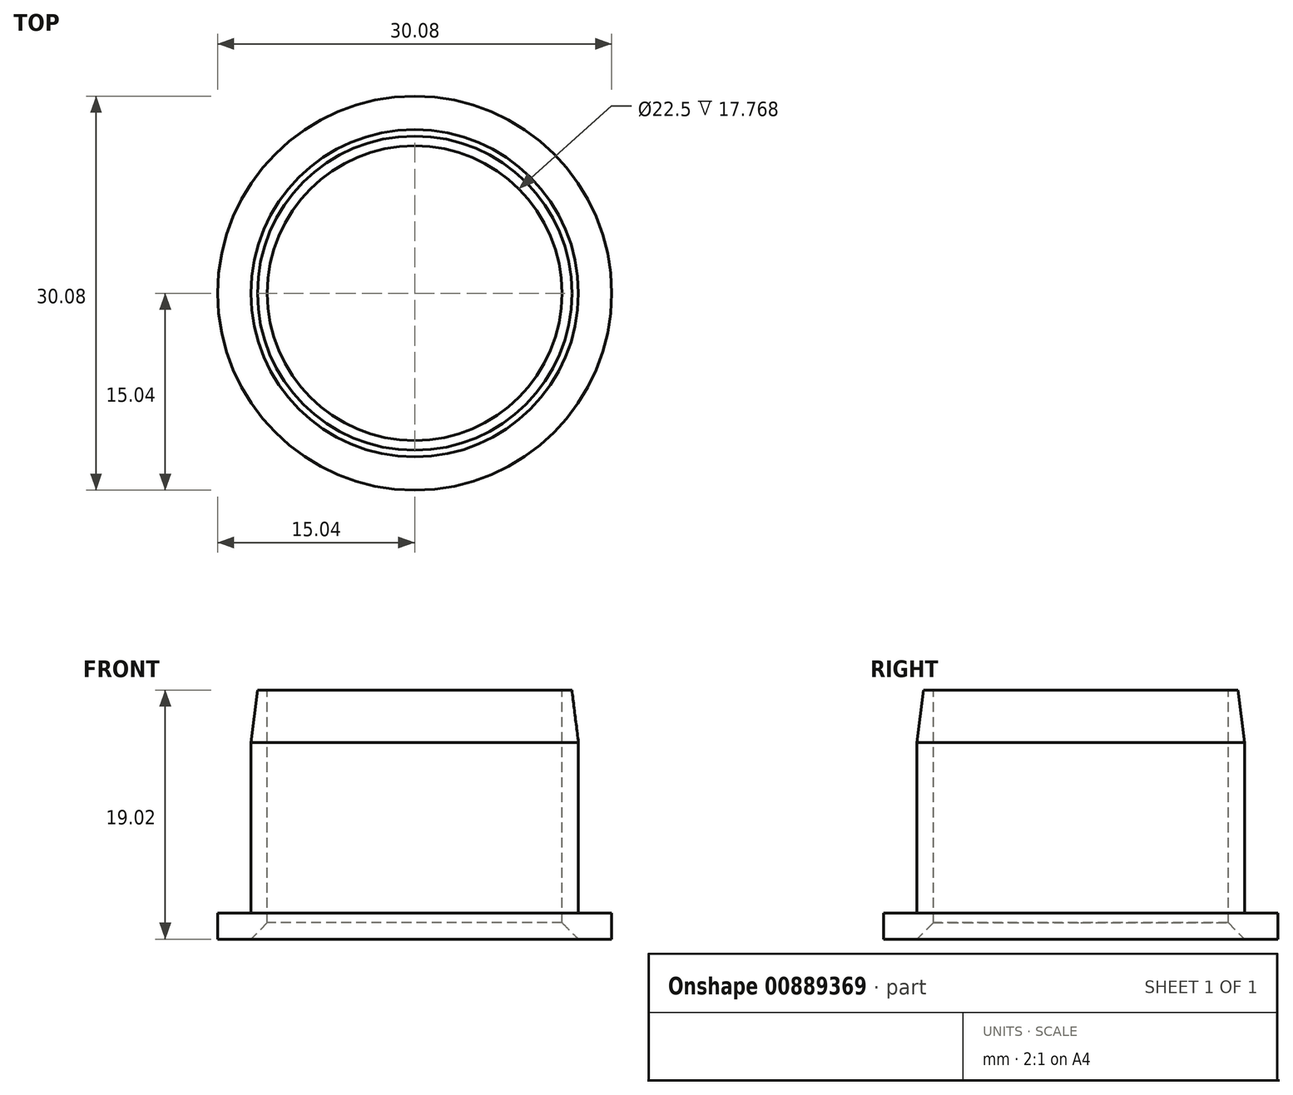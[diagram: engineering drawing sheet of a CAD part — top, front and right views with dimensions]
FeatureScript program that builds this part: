
annotation { "Feature Type Name" : "Feature", "Feature Type Description" : "" }
export const myFeature = defineFeature(function(context is Context, id is Id, definition is map)
    precondition{}
    {
        {
            assignVariable(context, id + "F0", {"name" : "H", "anyValue" : 17.02 * mm});
        }
        {
            var Q0;
            Q0=qCreatedBy(makeId("Top.planeOp"),FACE);
            var sketch = newSketch(context, id + "F1", { "sketchPlane" : qUnion([Q0])});
            skCircle(sketch, "E0", {"center": v(0, 0) * mm, "radius": 12.5 * mm});
            skCircle(sketch, "E1", {"center": v(0, 0) * mm, "radius": 11.25 * mm});
            skCircle(sketch, "E2", {"center": v(0, 0) * mm, "radius": 15.04 * mm});
            skSolve(sketch);
        }
        {
            var Q0;
            Q0=makeQuery(id+"F1.imprint","IMPRINT",FACE,{"disambiguationData":[TD([[makeQuery(id+"F1.imprint","IMPRINT",EDGE,{"derivedFrom":sQuery(id+"F1.wireOp",EDGE,"E0")}),-1.0]])]});
            var Q1;
            Q1=makeQuery(id+"F1.imprint","IMPRINT",FACE,{"disambiguationData":[TD([[makeQuery(id+"F1.imprint","IMPRINT",EDGE,{"derivedFrom":sQuery(id+"F1.wireOp",EDGE,"E0")}),1.0]])]});
            extrude(context, id + "F2", {"entities" : qUnion([Q0, Q1]), "oppositeDirection" : true, "depth" : 2 * mm, "offsetDistance" : 25.4 * mm});
        }
        {
            var Q0;
            Q0=makeQuery(id+"F1.imprint","IMPRINT",FACE,{"disambiguationData":[TD([[makeQuery(id+"F1.imprint","IMPRINT",EDGE,{"derivedFrom":sQuery(id+"F1.wireOp",EDGE,"E0")}),1.0]])]});
            extrude(context, id + "F3", {"entities" : qUnion([Q0]), "operationType" : NewBodyOperationType.ADD, "depth" : getVariable(context, 'H'), "offsetDistance" : 25.4 * mm});
        }
        {
            var Q0;
            Q0=makeQuery(id+"F3.opExtrude","CAP_EDGE",EDGE,{"disambiguationData":[OSD([sQuery(id+"F1.wireOp",EDGE,"E0")])],"isStart":false});
            chamfer(context, id + "F4", {"entities" : qUnion([Q0]), "chamferType" : ChamferType.TWO_OFFSETS, "width1" : 0.5 * mm, "oppositeDirection" : false, "width2" : 4 * mm, "tangentPropagation" : true});
        }
        {
            var Q0;
            Q0=makeQuery(id+"F2.opExtrude","CAP_EDGE",EDGE,{"disambiguationData":[OSD([sQuery(id+"F1.wireOp",EDGE,"E1")])],"isStart":false});
            chamfer(context, id + "F5", {"entities" : qUnion([Q0]), "width" : 1.25 * mm, "tangentPropagation" : true});
        }
    });
